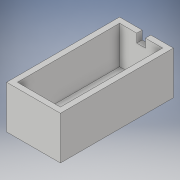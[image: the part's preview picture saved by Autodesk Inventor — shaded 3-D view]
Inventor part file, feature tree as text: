
AUTODESK INVENTOR PART (.ipt)
format: ipt  version: 2017 (Build 210142000, 142)  size: 132,608 bytes
history: native  units: in
note: dims shown in document units (in); Inventor stores cm internally (conversion verified against a paired STEP export)
features: extrude x6, sketch x6
ambient origin geometry x8: Origin, YZ Plane, XZ Plane, XY Plane, X Axis, Y Axis, Z Axis, Center Point
bodies: Solid1 (feature_tree)
feature tree (12):
  extrude  "Extrusion1"  Depth=2.0in
  extrude  "Extrusion2"  Depth=0.4in
  extrude  "Extrusion3"  Depth=5.25in
  extrude  "Extrusion4"  Depth=0.25in TaperAngle=0.0deg
  extrude  "Extrusion5"  Depth=2.0in TaperAngle=0.0deg
  extrude  "Extrusion6"  [1 undecoded]
  sketch  "Sketch1"  dims[d0=2.0in d1=2.0in]
  sketch  "Sketch2"  dims[d2=0.25in d3=0.0in d4=0.4in]
  sketch  "Sketch3"  dims[d5=0.4in d6=0.0in d7=5.25in]
  sketch  "Sketch4"  dims[d8=0.25in d9=0.0in d10=0.25in d11=0.0in]
  sketch  "Sketch5"  dims[d12=0.25in d13=2.0in d14=0.0in]
  sketch  "Sketch6"  dims[d15=0.25in d16=0.0in]
note: 1 required parameter value undecoded (feature->parameter linkage not recoverable at this tier; creation-order binding heuristic only, values carry confidence <= 0.55)
